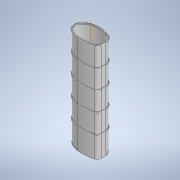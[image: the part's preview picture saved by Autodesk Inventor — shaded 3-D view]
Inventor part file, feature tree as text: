
AUTODESK INVENTOR PART (.ipt)
format: ipt  version: 2022 (Build 260153070, 153G)  size: 536,576 bytes
history: native  units: mm
features: extrude x3, sketch x3, other x2, fillet x2, projected_geometry x2, shell x1, thicken_offset x1, pattern_linear x1
ambient origin geometry x8: Origin, YZ Plane, XZ Plane, XY Plane, X Axis, Y Axis, Z Axis, Center Point
bodies: Solid3 (feature_tree), Solid4 (feature_tree)
feature tree (15):
  extrude  "Extrusion4"  Depth=300.0mm
  shell  "Shell1"  Thickness=21.0mm
  other  "Work Axis1"
  fillet  "Fillet2"  Radius=300.0mm
  extrude  "Extrusion5"  Depth=5.0mm
  other  "Work Point1"
  extrude  "Extrusion6"  Depth=46.0mm
  thicken_offset  "Thicken1"
  fillet  "Fillet3"  Radius=5.0mm
  pattern_linear  "Rectangular Pattern1"  Spacing1=5.0mm  [1 undecoded]
  sketch  "Sketch2"  dims[d9=10.0mm d10=120.0mm d11=21.0mm d12=300.0mm d13=0.0mm]
  sketch  "Sketch6"  dims[d14=2.0mm d16=5.0mm]
  projected_geometry  "Projected Loop1"
  sketch  "Sketch7"  dims[d19=5.0mm d20=5.0mm d21=5.0mm d22=5.0mm d23=5.0mm d24=3.0mm d25=0.0mm d26=28.0mm d27=46.0mm d28=3.0mm d29=0.0mm d30=2.0mm d31=2.0mm d33=1.5mm d34=50.0mm d36=60.0mm]
  projected_geometry  "Projected Loop2"
note: 1 required parameter value undecoded (feature->parameter linkage not recoverable at this tier; creation-order binding heuristic only, values carry confidence <= 0.55)
